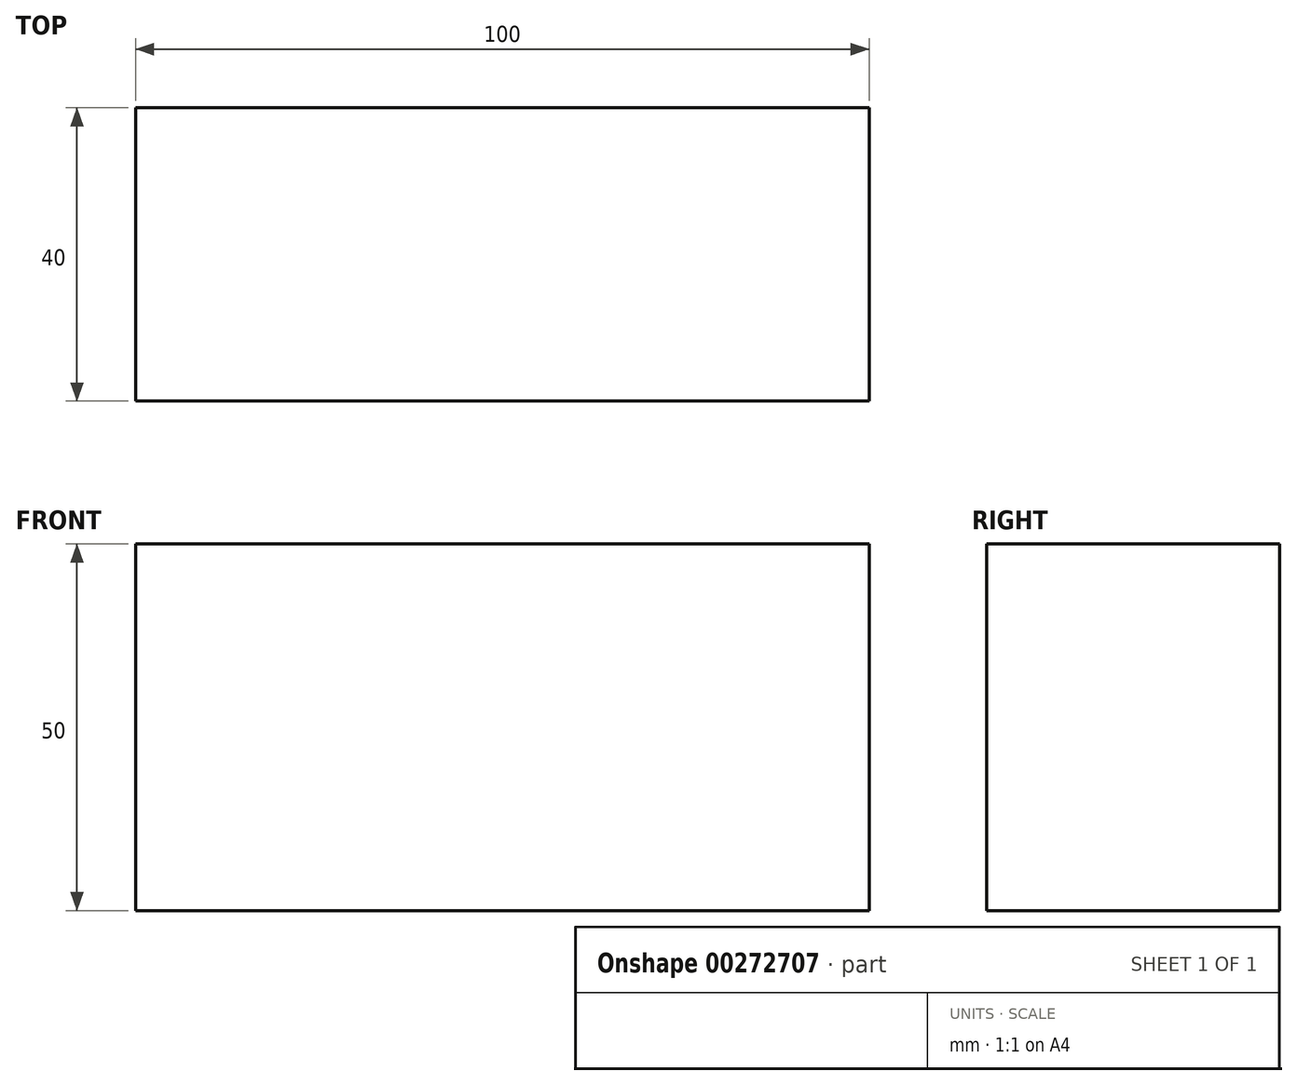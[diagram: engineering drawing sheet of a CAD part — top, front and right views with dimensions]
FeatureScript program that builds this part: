
annotation { "Feature Type Name" : "Feature", "Feature Type Description" : "" }
export const myFeature = defineFeature(function(context is Context, id is Id, definition is map)
    precondition{}
    {
        {
            var Q0;
            Q0=qCreatedBy(makeId("Top.planeOp"),FACE);
            var sketch = newSketch(context, id + "F0", { "sketchPlane" : qUnion([Q0])});
            skLineSegment(sketch, "E0.bottom", {"start": v(50, -20) * mm, "end": v(-50, -20) * mm});
            skLineSegment(sketch, "E0.top", {"start": v(50, 20) * mm, "end": v(-50, 20) * mm});
            skLineSegment(sketch, "E0.left", {"start": v(50, -20) * mm, "end": v(50, 20) * mm});
            skLineSegment(sketch, "E0.right", {"start": v(-50, -20) * mm, "end": v(-50, 20) * mm});
            skPoint(sketch, "E0.middle", {"position": v(0, 0) * mm});
            skSolve(sketch);
        }
        {
            var Q0;
            Q0=makeQuery(id+"F0.imprint","IMPRINT",FACE,{"disambiguationData":[TD([[makeQuery(id+"F0.imprint","IMPRINT",EDGE,{"derivedFrom":sQuery(id+"F0.wireOp",EDGE,"E0.bottom")}),-1.0]])]});
            extrude(context, id + "F1", {"entities" : qUnion([Q0]), "depth" : 50 * mm});
        }
    });
